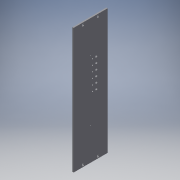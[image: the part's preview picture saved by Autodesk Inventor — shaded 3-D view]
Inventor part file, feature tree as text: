
AUTODESK INVENTOR PART (.ipt)
format: ipt  version: 2018 (Build 220112000, 112)  size: 218,112 bytes
history: native  units: mm
features: extrude x2, sketch x2
ambient origin geometry x8: Origin, YZ Plane, XZ Plane, XY Plane, X Axis, Y Axis, Z Axis, Center Point
bodies: Solid1 (feature_tree)
feature tree (4):
  extrude  "Extrusion1"  Depth=485.0mm
  extrude  "Extrusion2"  Depth=10.0mm
  sketch  "Sketch1"  dims[d0=132.0mm d1=485.0mm]
  sketch  "Sketch2"  dims[d2=5.0mm d3=0.0mm d4=10.48mm d7=28.87mm d10=234.34mm d11=5.24mm d12=6.93mm d13=20.0mm d15=468.68mm d16=20.0mm d18=57.74mm d21=242.0mm d22=85.0mm d23=117.9mm d24=42.5mm d25=3.3mm d26=20.0mm d28=235.8mm d29=10.0mm d31=10.0mm d33=117.9mm d34=8.1mm d35=5.0mm d37=20.0mm d38=18.0mm d39=15.0mm d40=4.05mm d41=7.1mm d42=60.0mm d44=22.0mm d45=10.0mm d47=10.0mm d49=5.0mm d50=0.0mm d51=452.563mm d52=452.563mm d53=7.42mm d54=15.08mm d55=187.0mm d56=4.2mm d57=8.0mm d58=4.2mm d59=8.0mm d61=20.0mm d63=20.0mm d65=20.0mm d67=10.0mm d69=60.0mm d71=10.0mm d72=15.08mm d73=187.0mm d74=4.2mm d76=4.2mm d78=7.42mm d79=8.0mm d80=8.0mm]
